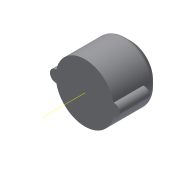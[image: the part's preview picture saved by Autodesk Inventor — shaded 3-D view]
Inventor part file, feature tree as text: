
AUTODESK INVENTOR PART (.ipt)
format: ipt  version: 2014 (Build 180170000, 170)  size: 126,464 bytes
history: native  units: mm
features: extrude x2, fillet x2, sketch x2, chamfer x1, other x1
ambient origin geometry x8: Origin, YZ Plane, XZ Plane, XY Plane, X Axis, Y Axis, Z Axis, Center Point
bodies: Volumenkörper1 (feature_tree)
feature tree (8):
  extrude  "Extrusion1"  Depth=3.0mm
  extrude  "Extrusion2"  Depth=0.5mm TaperAngle=0.0deg
  chamfer  "Fase1"  Distance=3.0mm
  fillet  "Rundung1"  Radius=3.0mm
  fillet  "Rundung2"  Radius=8.0mm
  other  "Arbeitsachse1"
  sketch  "Skizze1"  dims[d0=15.0mm d1=3.0mm]
  sketch  "Skizze2"  dims[d2=3.0mm d3=12.0mm d4=0.0mm d5=3.0mm d6=3.0mm d7=8.0mm d8=0.0mm d9=2.0mm d10=2.0mm d11=45.0deg d12=1.0mm d13=0.5mm]
